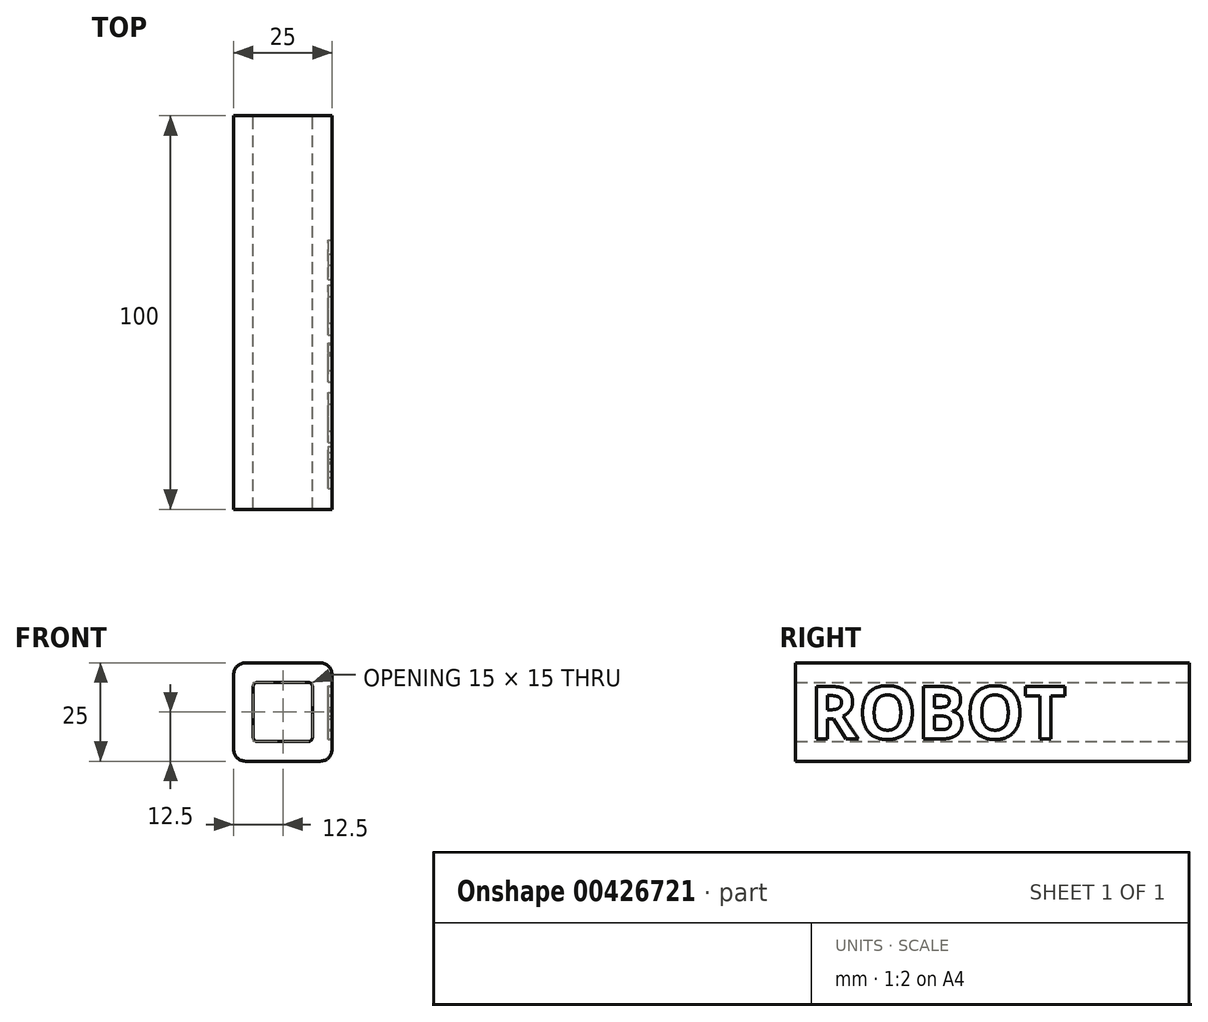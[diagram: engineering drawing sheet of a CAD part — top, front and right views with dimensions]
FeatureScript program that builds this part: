
annotation { "Feature Type Name" : "Feature", "Feature Type Description" : "" }
export const myFeature = defineFeature(function(context is Context, id is Id, definition is map)
    precondition{}
    {
        {
            var Q0;
            Q0=qCreatedBy(makeId("Front.planeOp"),FACE);
            var sketch = newSketch(context, id + "F0", { "sketchPlane" : qUnion([Q0])});
            skLineSegment(sketch, "E0.bottom", {"start": v(-12.5, 12.5) * mm, "end": v(12.5, 12.5) * mm});
            skLineSegment(sketch, "E0.top", {"start": v(-12.5, -12.5) * mm, "end": v(12.5, -12.5) * mm});
            skLineSegment(sketch, "E0.left", {"start": v(-12.5, 12.5) * mm, "end": v(-12.5, -12.5) * mm});
            skLineSegment(sketch, "E0.right", {"start": v(12.5, 12.5) * mm, "end": v(12.5, -12.5) * mm});
            skPoint(sketch, "E0.middle", {"position": v(0, 0) * mm});
            skLineSegment(sketch, "E1.bottom", {"start": v(-7.5, 7.5) * mm, "end": v(7.5, 7.5) * mm});
            skLineSegment(sketch, "E1.top", {"start": v(-7.5, -7.5) * mm, "end": v(7.5, -7.5) * mm});
            skLineSegment(sketch, "E1.left", {"start": v(-7.5, 7.5) * mm, "end": v(-7.5, -7.5) * mm});
            skLineSegment(sketch, "E1.right", {"start": v(7.5, 7.5) * mm, "end": v(7.5, -7.5) * mm});
            skSolve(sketch);
        }
        {
            var Q0;
            Q0 = qSketchRegion(id + "F0", true);
            extrude(context, id + "F1", {"entities" : qUnion([Q0]), "depth" : 100 * mm});
        }
        {
            var Q0;
            Q0=makeQuery(id+"F1.opExtrude","SWEPT_EDGE",EDGE,{"disambiguationData":[OSD([sQuery(id+"F0.wireOp",EDGE,"E1.bottom"),sQuery(id+"F0.wireOp",EDGE,"E1.left")])]});
            var Q1;
            Q1=makeQuery(id+"F1.opExtrude","SWEPT_EDGE",EDGE,{"disambiguationData":[OSD([sQuery(id+"F0.wireOp",EDGE,"E1.bottom"),sQuery(id+"F0.wireOp",EDGE,"E1.right")])]});
            var Q2;
            Q2=makeQuery(id+"F1.opExtrude","SWEPT_EDGE",EDGE,{"disambiguationData":[OSD([sQuery(id+"F0.wireOp",EDGE,"E1.top"),sQuery(id+"F0.wireOp",EDGE,"E1.right")])]});
            var Q3;
            Q3=makeQuery(id+"F1.opExtrude","SWEPT_EDGE",EDGE,{"disambiguationData":[OSD([sQuery(id+"F0.wireOp",EDGE,"E1.top"),sQuery(id+"F0.wireOp",EDGE,"E1.left")])]});
            fillet(context, id + "F2", {"entities" : qUnion([Q0, Q1, Q2, Q3]), "radius" : 1 * mm, "tangentPropagation" : true, "allowEdgeOverflow" : false});
        }
        {
            var Q0;
            Q0=makeQuery(id+"F1.opExtrude","SWEPT_EDGE",EDGE,{"disambiguationData":[OSD([sQuery(id+"F0.wireOp",EDGE,"E0.bottom"),sQuery(id+"F0.wireOp",EDGE,"E0.right")])]});
            var Q1;
            Q1=makeQuery(id+"F1.opExtrude","SWEPT_EDGE",EDGE,{"disambiguationData":[OSD([sQuery(id+"F0.wireOp",EDGE,"E0.bottom"),sQuery(id+"F0.wireOp",EDGE,"E0.left")])]});
            var Q2;
            Q2=makeQuery(id+"F1.opExtrude","SWEPT_EDGE",EDGE,{"disambiguationData":[OSD([sQuery(id+"F0.wireOp",EDGE,"E0.top"),sQuery(id+"F0.wireOp",EDGE,"E0.left")])]});
            var Q3;
            Q3=makeQuery(id+"F1.opExtrude","SWEPT_EDGE",EDGE,{"disambiguationData":[OSD([sQuery(id+"F0.wireOp",EDGE,"E0.top"),sQuery(id+"F0.wireOp",EDGE,"E0.right")])]});
            fillet(context, id + "F3", {"entities" : qUnion([Q0, Q1, Q2, Q3]), "radius" : 3 * mm, "tangentPropagation" : true, "allowEdgeOverflow" : false});
        }
        {
            var Q0;
            Q0=makeQuery(id+"F1.opExtrude","SWEPT_FACE",FACE,{"disambiguationData":[OSD([sQuery(id+"F0.wireOp",EDGE,"E0.right")])]});
            var sketch = newSketch(context, id + "F4", { "sketchPlane" : qUnion([Q0])});
            skText(sketch, "E2", { "text": "ROBOT", "fontName": "OpenSans-Bold.ttf"});
            const initialGuessF4  = {"E2": [-0.09637, -0.00681, 1, 0, 0.0134]};
            skSetInitialGuess(sketch, initialGuessF4);
            skSolve(sketch);
        }
        {
            var Q0;
            Q0 = qSketchRegion(id + "F4", true);
            extrude(context, id + "F5", {"entities" : qUnion([Q0]), "operationType" : NewBodyOperationType.REMOVE, "oppositeDirection" : true, "depth" : 1 * mm});
        }
    });
